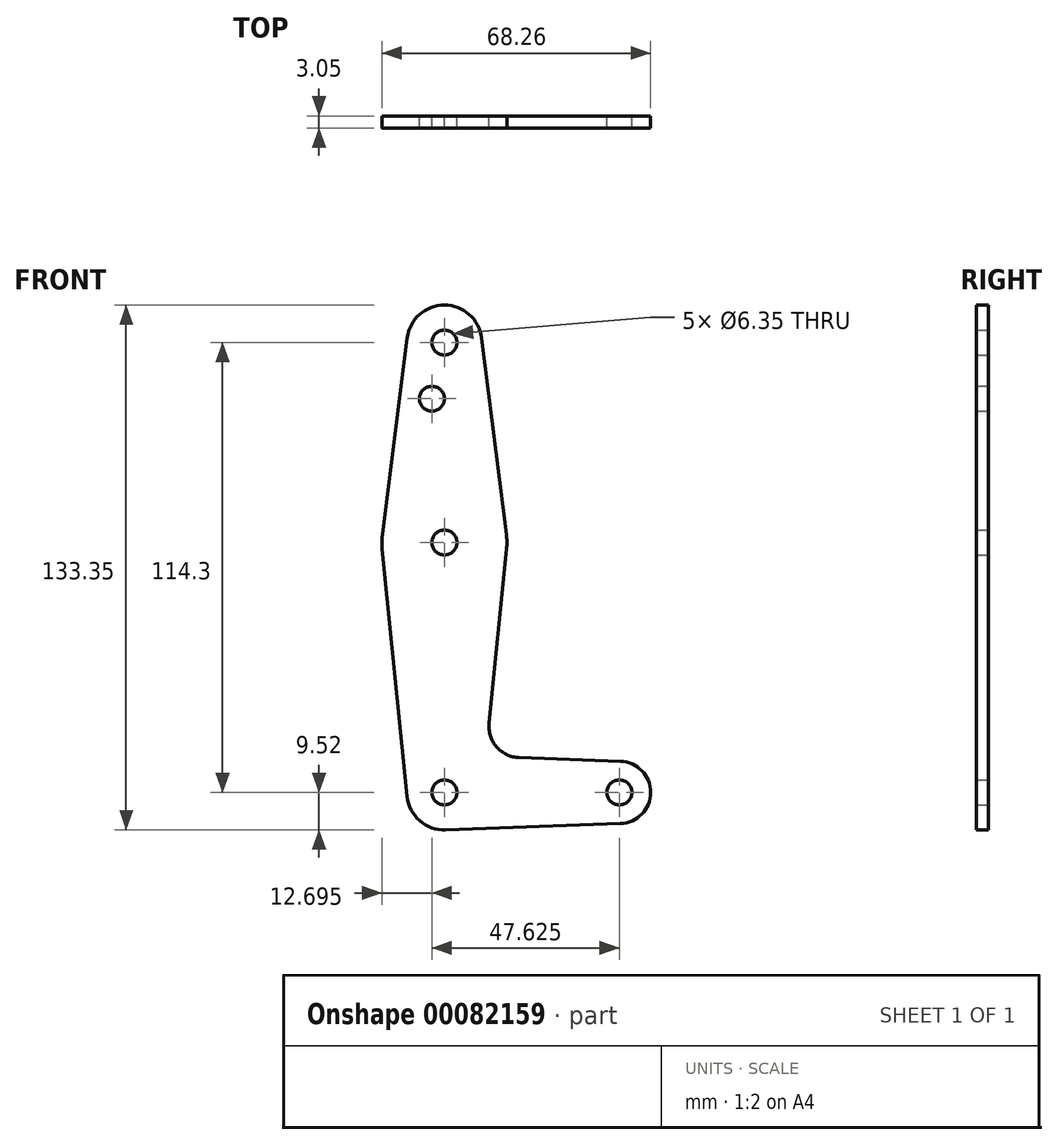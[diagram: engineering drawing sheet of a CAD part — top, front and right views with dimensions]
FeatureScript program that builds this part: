
annotation { "Feature Type Name" : "Feature", "Feature Type Description" : "" }
export const myFeature = defineFeature(function(context is Context, id is Id, definition is map)
    precondition{}
    {
        {
            var Q0;
            Q0=qCreatedBy(makeId("Front.planeOp"),FACE);
            var sketch = newSketch(context, id + "F0", { "sketchPlane" : qUnion([Q0])});
            skLineSegment(sketch, "E0", {"start": v(0, 0) * mm, "end": v(0, 114.3) * mm, "construction": true});
            skLineSegment(sketch, "E1", {"start": v(0, 0) * mm, "end": v(44.45, 0) * mm, "construction": true});
            skCircle(sketch, "E2", {"center": v(0, 114.3) * mm, "radius": 9.53 * mm});
            skCircle(sketch, "E3", {"center": v(0, 0) * mm, "radius": 9.53 * mm});
            skCircle(sketch, "E4", {"center": v(44.45, 0) * mm, "radius": 7.94 * mm});
            skCircle(sketch, "E5", {"center": v(0, 63.5) * mm, "radius": 15.88 * mm});
            skLineSegment(sketch, "E6", {"start": v(-9.45, 115.5) * mm, "end": v(-15.75, 65.48) * mm});
            skLineSegment(sketch, "E7", {"start": v(-15.8, 61.91) * mm, "end": v(-9.48, -0.95) * mm});
            skLineSegment(sketch, "E8", {"start": v(0.34, -9.52) * mm, "end": v(44.73, -7.93) * mm});
            skLineSegment(sketch, "E9", {"start": v(18.97, 8.85) * mm, "end": v(44.73, 7.93) * mm});
            skLineSegment(sketch, "E10", {"start": v(15.8, 61.91) * mm, "end": v(11.34, 17.6) * mm});
            skLineSegment(sketch, "E11", {"start": v(9.45, 115.5) * mm, "end": v(15.75, 65.48) * mm});
            skArc(sketch, "E12.filletArc", {"start": v(11.34, 17.6) * mm, "mid": v(13.26, 11.57) * mm, "end": v(18.97, 8.85) * mm});
            skCircle(sketch, "E13", {"center": v(-3.18, 100.03) * mm, "radius": 3.18 * mm});
            skCircle(sketch, "E14", {"center": v(0, 114.3) * mm, "radius": 3.18 * mm});
            skCircle(sketch, "E15", {"center": v(0, 63.5) * mm, "radius": 3.18 * mm});
            skCircle(sketch, "E16", {"center": v(0, 0) * mm, "radius": 3.18 * mm});
            skCircle(sketch, "E17", {"center": v(44.45, 0) * mm, "radius": 3.18 * mm});
            skSolve(sketch);
        }
        {
            var Q0;
            Q0=makeQuery(id+"F0.imprint","IMPRINT",FACE,{"disambiguationData":[TD([[makeQuery(id+"F0.imprint","IMPRINT",EDGE,{"derivedFrom":sQuery(id+"F0.wireOp",EDGE,"E14")}),-1.0]])]});
            var Q1;
            {var subQ1=sQuery(id+"F0.wireOp",EDGE,"E6");Q1=makeQuery(id+"F0.imprint","IMPRINT",FACE,{"disambiguationData":[TD([[makeQuery(id+"F0.imprint","IMPRINT",EDGE,{"derivedFrom":subQ1}),1.0]])]});}
            var Q2;
            Q2=makeQuery(id+"F0.imprint","IMPRINT",FACE,{"disambiguationData":[TD([[makeQuery(id+"F0.imprint","IMPRINT",EDGE,{"derivedFrom":sQuery(id+"F0.wireOp",EDGE,"E15")}),-1.0]])]});
            var Q3;
            {var subQ0=sQuery(id+"F0.wireOp",EDGE,"E7");Q3=makeQuery(id+"F0.imprint","IMPRINT",FACE,{"disambiguationData":[TD([[makeQuery(id+"F0.imprint","IMPRINT",EDGE,{"derivedFrom":subQ0}),1.0]])]});}
            var Q4;
            Q4=makeQuery(id+"F0.imprint","IMPRINT",FACE,{"disambiguationData":[TD([[makeQuery(id+"F0.imprint","IMPRINT",EDGE,{"derivedFrom":sQuery(id+"F0.wireOp",EDGE,"E16")}),-1.0]])]});
            var Q5;
            Q5=makeQuery(id+"F0.imprint","IMPRINT",FACE,{"disambiguationData":[TD([[makeQuery(id+"F0.imprint","IMPRINT",EDGE,{"derivedFrom":sQuery(id+"F0.wireOp",EDGE,"E17")}),-1.0]])]});
            extrude(context, id + "F1", {"entities" : qUnion([Q0, Q1, Q2, Q3, Q4, Q5]), "depth" : 3.05 * mm});
        }
    });
